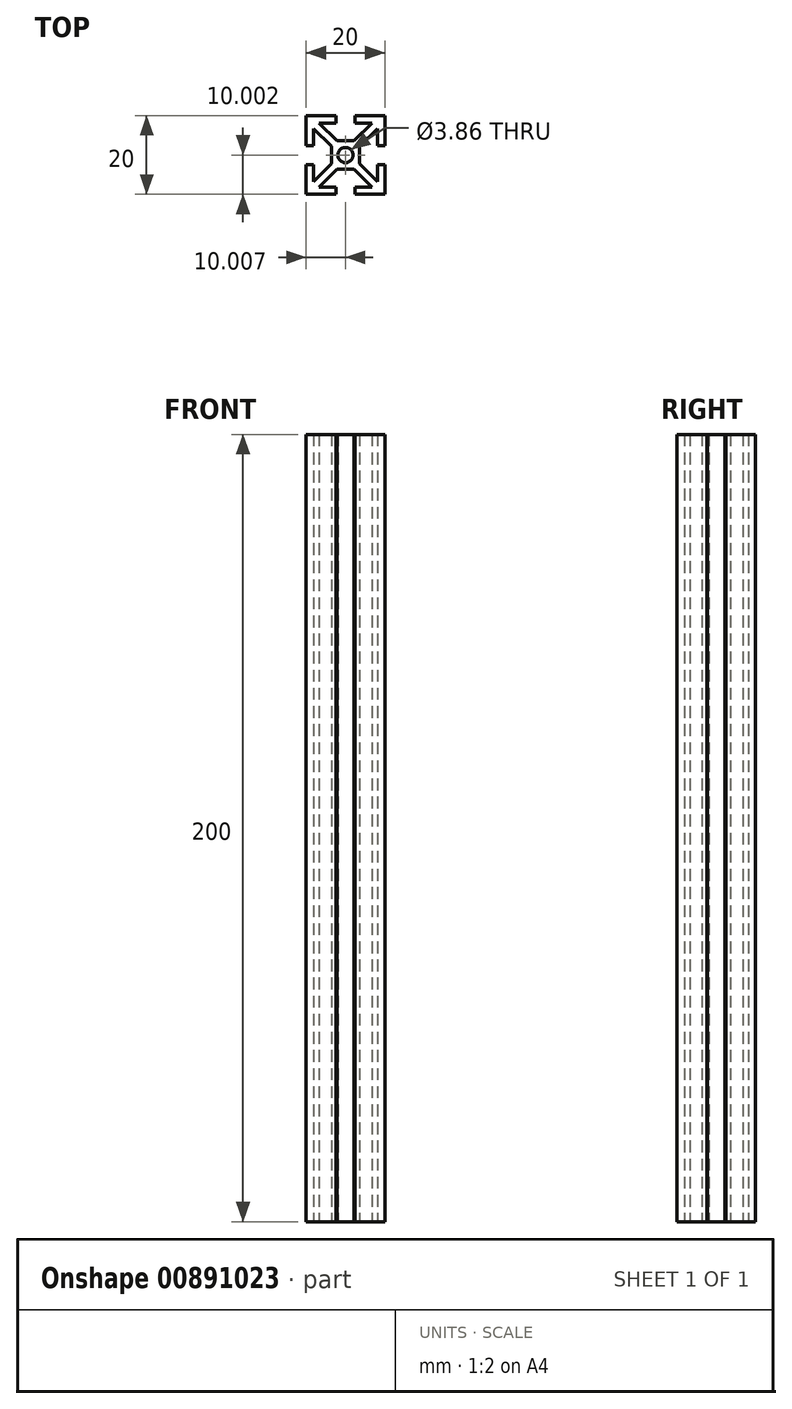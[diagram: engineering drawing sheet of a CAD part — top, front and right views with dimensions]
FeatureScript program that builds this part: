
annotation { "Feature Type Name" : "Feature", "Feature Type Description" : "" }
export const myFeature = defineFeature(function(context is Context, id is Id, definition is map)
    precondition{}
    {
        {
            var Q0;
            Q0=qCreatedBy(makeId("Top.planeOp"),FACE);
            var sketch = newSketch(context, id + "F0", { "sketchPlane" : qUnion([Q0])});
            skPoint(sketch, "E0.0", {"position": v(2.4, 9.96) * mm});
            skPoint(sketch, "E0.1", {"position": v(2.4, 8.1) * mm});
            skPoint(sketch, "E0.2", {"position": v(10.02, 9.96) * mm});
            skPoint(sketch, "E0.3", {"position": v(10.02, 2.35) * mm});
            skPoint(sketch, "E0.4", {"position": v(8.13, 2.35) * mm});
            skPoint(sketch, "E0.5", {"position": v(8.13, 6.7) * mm});
            skPoint(sketch, "E0.6", {"position": v(6.75, 8.1) * mm});
            skPoint(sketch, "E0.7", {"position": v(2.23, 3.57) * mm});
            skPoint(sketch, "E0.8", {"position": v(-2.18, 3.57) * mm});
            skPoint(sketch, "E0.9", {"position": v(3.63, 2.2) * mm});
            skPoint(sketch, "E0.10", {"position": v(3.63, -2.28) * mm});
            skPoint(sketch, "E0.11", {"position": v(-6.7, 8.1) * mm});
            skPoint(sketch, "E0.12", {"position": v(-8.09, 6.7) * mm});
            skPoint(sketch, "E0.13", {"position": v(-8.09, 2.35) * mm});
            skPoint(sketch, "E0.14", {"position": v(-9.98, 2.35) * mm});
            skPoint(sketch, "E0.15", {"position": v(-9.98, 9.96) * mm});
            skPoint(sketch, "E0.16", {"position": v(-2.35, 9.96) * mm});
            skPoint(sketch, "E0.17", {"position": v(-2.35, 8.1) * mm});
            skPoint(sketch, "E0.18", {"position": v(-3.59, 2.2) * mm});
            skPoint(sketch, "E0.19", {"position": v(-3.59, -2.28) * mm});
            skPoint(sketch, "E0.20", {"position": v(-8.09, -6.78) * mm});
            skPoint(sketch, "E0.21", {"position": v(-8.09, -2.42) * mm});
            skPoint(sketch, "E0.22", {"position": v(-9.98, -2.42) * mm});
            skPoint(sketch, "E0.23", {"position": v(-9.98, -10.04) * mm});
            skPoint(sketch, "E0.24", {"position": v(-2.36, -10.04) * mm});
            skPoint(sketch, "E0.25", {"position": v(-2.36, -8.17) * mm});
            skPoint(sketch, "E0.26", {"position": v(-6.7, -8.17) * mm});
            skPoint(sketch, "E0.27", {"position": v(-2.18, -3.65) * mm});
            skPoint(sketch, "E0.28", {"position": v(2.23, -3.65) * mm});
            skPoint(sketch, "E0.29", {"position": v(6.74, -8.17) * mm});
            skPoint(sketch, "E0.30", {"position": v(2.4, -8.17) * mm});
            skPoint(sketch, "E0.31", {"position": v(2.4, -10.04) * mm});
            skPoint(sketch, "E0.32", {"position": v(10.02, -10.04) * mm});
            skPoint(sketch, "E0.33", {"position": v(10.02, -2.42) * mm});
            skPoint(sketch, "E0.34", {"position": v(8.13, -2.42) * mm});
            skPoint(sketch, "E0.35", {"position": v(8.13, -6.78) * mm});
            skLineSegment(sketch, "E1", {"start": v(-9.98, 9.96) * mm, "end": v(-2.35, 9.96) * mm});
            skLineSegment(sketch, "E2", {"start": v(-2.35, 9.96) * mm, "end": v(-2.35, 8.1) * mm});
            skLineSegment(sketch, "E3", {"start": v(-2.35, 8.1) * mm, "end": v(-6.7, 8.1) * mm});
            skLineSegment(sketch, "E4", {"start": v(-6.7, 8.1) * mm, "end": v(-2.18, 3.57) * mm});
            skLineSegment(sketch, "E5", {"start": v(-2.18, 3.57) * mm, "end": v(2.23, 3.57) * mm});
            skLineSegment(sketch, "E6", {"start": v(2.23, 3.57) * mm, "end": v(6.75, 8.1) * mm});
            skLineSegment(sketch, "E7", {"start": v(2.4, 8.1) * mm, "end": v(6.75, 8.1) * mm});
            skLineSegment(sketch, "E8", {"start": v(2.4, 8.1) * mm, "end": v(2.4, 9.96) * mm});
            skLineSegment(sketch, "E9", {"start": v(2.4, 9.96) * mm, "end": v(10.02, 9.96) * mm});
            skLineSegment(sketch, "E10", {"start": v(10.02, 9.96) * mm, "end": v(10.02, 2.35) * mm});
            skLineSegment(sketch, "E11", {"start": v(10.02, 2.35) * mm, "end": v(8.13, 2.35) * mm});
            skLineSegment(sketch, "E12", {"start": v(8.13, 2.35) * mm, "end": v(8.13, 6.7) * mm});
            skLineSegment(sketch, "E13", {"start": v(8.13, 6.7) * mm, "end": v(3.63, 2.2) * mm});
            skLineSegment(sketch, "E14", {"start": v(3.63, 2.2) * mm, "end": v(3.63, -2.28) * mm});
            skLineSegment(sketch, "E15", {"start": v(3.63, -2.28) * mm, "end": v(8.13, -6.78) * mm});
            skLineSegment(sketch, "E16", {"start": v(8.13, -6.78) * mm, "end": v(8.13, -2.42) * mm});
            skLineSegment(sketch, "E17", {"start": v(8.13, -2.42) * mm, "end": v(10.02, -2.42) * mm});
            skLineSegment(sketch, "E18", {"start": v(10.02, -2.42) * mm, "end": v(10.02, -10.04) * mm});
            skLineSegment(sketch, "E19", {"start": v(10.02, -10.04) * mm, "end": v(2.4, -10.04) * mm});
            skLineSegment(sketch, "E20", {"start": v(2.4, -10.04) * mm, "end": v(2.4, -8.17) * mm});
            skLineSegment(sketch, "E21", {"start": v(2.4, -8.17) * mm, "end": v(6.74, -8.17) * mm});
            skLineSegment(sketch, "E22", {"start": v(6.74, -8.17) * mm, "end": v(2.23, -3.65) * mm});
            skLineSegment(sketch, "E23", {"start": v(2.23, -3.65) * mm, "end": v(-2.18, -3.65) * mm});
            skLineSegment(sketch, "E24", {"start": v(-2.18, -3.65) * mm, "end": v(-6.7, -8.17) * mm});
            skLineSegment(sketch, "E25", {"start": v(-6.7, -8.17) * mm, "end": v(-2.36, -8.17) * mm});
            skLineSegment(sketch, "E26", {"start": v(-2.36, -8.17) * mm, "end": v(-2.36, -10.04) * mm});
            skLineSegment(sketch, "E27", {"start": v(-2.36, -10.04) * mm, "end": v(-9.98, -10.04) * mm});
            skLineSegment(sketch, "E28", {"start": v(-9.98, -10.04) * mm, "end": v(-9.98, -2.42) * mm});
            skLineSegment(sketch, "E29", {"start": v(-9.98, -2.42) * mm, "end": v(-8.09, -2.42) * mm});
            skLineSegment(sketch, "E30", {"start": v(-8.09, -2.42) * mm, "end": v(-8.09, -6.78) * mm});
            skLineSegment(sketch, "E31", {"start": v(-8.09, -6.78) * mm, "end": v(-3.59, -2.28) * mm});
            skLineSegment(sketch, "E32", {"start": v(-3.59, -2.28) * mm, "end": v(-3.59, 2.2) * mm});
            skLineSegment(sketch, "E33", {"start": v(-3.59, 2.2) * mm, "end": v(-8.09, 6.7) * mm});
            skLineSegment(sketch, "E34", {"start": v(-8.09, 6.7) * mm, "end": v(-8.09, 2.35) * mm});
            skLineSegment(sketch, "E35", {"start": v(-8.09, 2.35) * mm, "end": v(-9.98, 2.35) * mm});
            skLineSegment(sketch, "E36", {"start": v(-9.98, 2.35) * mm, "end": v(-9.98, 9.96) * mm});
            skPoint(sketch, "E37.centerSnap0", {"position": v(0.03, 3.57) * mm});
            skPoint(sketch, "E37.centerSnap1", {"position": v(-3.59, -0.04) * mm});
            skPoint(sketch, "E38.0", {"position": v(1.8, -0.79) * mm});
            skCircle(sketch, "E39", {"center": v(0.03, -0.04) * mm, "radius": 1.93 * mm});
            skSolve(sketch);
        }
        {
            var Q0;
            Q0=makeQuery(id+"F0.imprint","IMPRINT",FACE,{"disambiguationData":[TD([[makeQuery(id+"F0.imprint","IMPRINT",EDGE,{"derivedFrom":sQuery(id+"F0.wireOp",EDGE,"E1")}),-1.0]])]});
            extrude(context, id + "F1", {"entities" : qUnion([Q0]), "depth" : 200 * mm, "offsetDistance" : 25 * mm});
        }
    });
